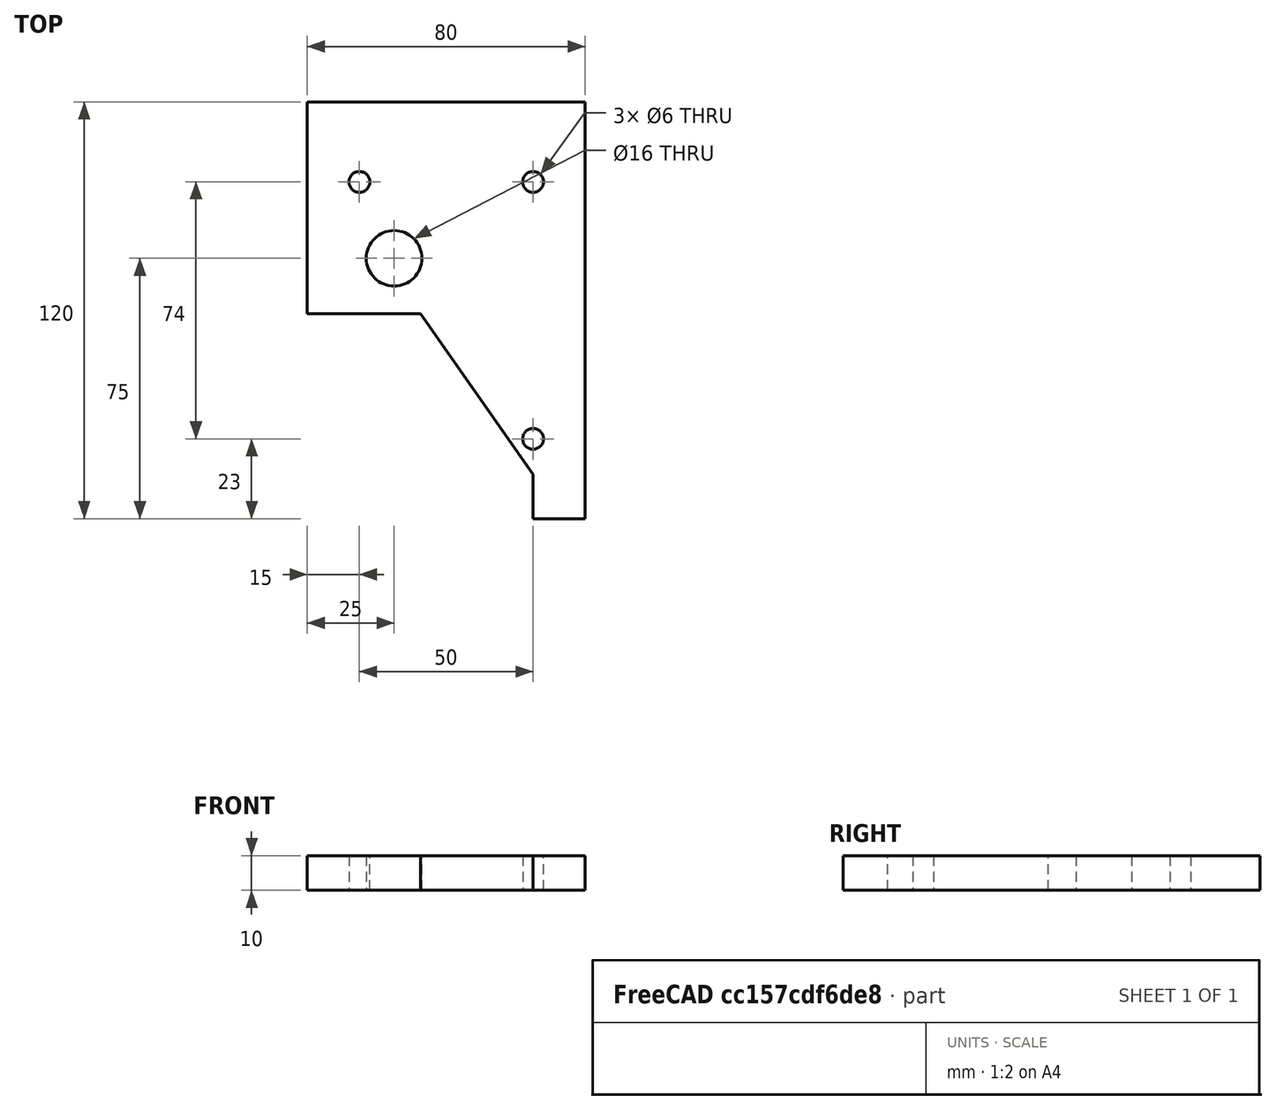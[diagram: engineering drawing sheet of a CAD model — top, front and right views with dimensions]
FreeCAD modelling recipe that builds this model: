
FCSTD DOCUMENT  (FreeCAD 0.19R24276 (Git))
Label: BLDC_holder_part4_up
License: All rights reserved
LicenseURL: http://en.wikipedia.org/wiki/All_rights_reserved
objects: Sketcher::SketchObject×1, PartDesign::Pad×1, PartDesign::Body×1
note: 4 computed .brp shape members not serialized (recipe doc carries the construction recipe); baked Part::Feature solids carry a one-line shape summary decoded from their .brp

FEATURE [Sketcher::SketchObject] Sketch  label="Sketch_L80x120"
  FullyConstrained = false
  MapMode = 5
  Support = -> [XY_Plane]
  sketch-geometry (36):
    g0: Circle CenterX=0 CenterY=0 CenterZ=0 NormalX=0 NormalY=0 NormalZ=1 AngleXU=0 Radius=8
    g1: Circle CenterX=0 CenterY=-30 CenterZ=0 NormalX=0 NormalY=0 NormalZ=1 AngleXU=0 Radius=11
    g2: LineSegment StartX=-25 StartY=45 StartZ=0 EndX=55 EndY=45 EndZ=0
    g3: LineSegment StartX=55 StartY=45 StartZ=0 EndX=55 EndY=-75 EndZ=0
    g4: LineSegment StartX=55 StartY=-75 StartZ=0 EndX=-25 EndY=-75 EndZ=0
    g5: LineSegment StartX=-25 StartY=-75 StartZ=0 EndX=-25 EndY=45 EndZ=0
    g6: Circle CenterX=-10 CenterY=-52 CenterZ=0 NormalX=0 NormalY=0 NormalZ=1 AngleXU=0 Radius=3
    g7: Circle CenterX=40 CenterY=-52 CenterZ=0 NormalX=0 NormalY=0 NormalZ=1 AngleXU=0 Radius=3
    g8: Circle CenterX=40 CenterY=22 CenterZ=0 NormalX=0 NormalY=0 NormalZ=1 AngleXU=0 Radius=3
    g9: Circle CenterX=-10 CenterY=22 CenterZ=0 NormalX=0 NormalY=0 NormalZ=1 AngleXU=0 Radius=3
    g10: Circle CenterX=0 CenterY=0 CenterZ=0 NormalX=0 NormalY=0 NormalZ=1 AngleXU=0 Radius=11
    g11: LineSegment StartX=14.5 StartY=-15.5 StartZ=0 EndX=-14.5 EndY=-15.5 EndZ=0
    g12: LineSegment StartX=-14.5 StartY=-15.5 StartZ=0 EndX=-14.5 EndY=-44.5 EndZ=0
    g13: LineSegment StartX=-14.5 StartY=-44.5 StartZ=0 EndX=14.5 EndY=-44.5 EndZ=0
    g14: LineSegment StartX=14.5 StartY=-44.5 StartZ=0 EndX=14.5 EndY=-15.5 EndZ=0
    g15: Circle CenterX=0 CenterY=-30 CenterZ=0 NormalX=0 NormalY=0 NormalZ=1 AngleXU=0 Radius=20.5061
    g16: LineSegment StartX=-44.3555 StartY=-59 StartZ=0 EndX=66.9363 EndY=-59 EndZ=0
    g17: LineSegment StartX=66.9363 StartY=-59 StartZ=0 EndX=66.9363 EndY=-67 EndZ=0
    g18: LineSegment StartX=66.9363 StartY=-67 StartZ=0 EndX=-44.3555 EndY=-67 EndZ=0
    g19: LineSegment StartX=-44.3555 StartY=-67 StartZ=0 EndX=-44.3555 EndY=-59 EndZ=0
    g20: LineSegment StartX=-44.3555 StartY=-63 StartZ=0 EndX=70.3737 EndY=-63 EndZ=0
    g21: LineSegment StartX=-44.3555 StartY=29 StartZ=0 EndX=66.9363 EndY=29 EndZ=0
    g22: LineSegment StartX=66.9363 StartY=29 StartZ=0 EndX=66.9363 EndY=37 EndZ=0
    g23: LineSegment StartX=66.9363 StartY=37 StartZ=0 EndX=-44.3555 EndY=37 EndZ=0
    g24: LineSegment StartX=-44.3555 StartY=37 StartZ=0 EndX=-44.3555 EndY=29 EndZ=0
    g25: LineSegment StartX=-44.3555 StartY=33 StartZ=0 EndX=70.3737 EndY=33 EndZ=0
    g26: LineSegment StartX=9.01067 StartY=-23.6907 StartZ=0 EndX=44.9379 EndY=-75 EndZ=0
    g27: LineSegment StartX=0 StartY=-30 StartZ=0 EndX=9.01067 EndY=-23.6907 EndZ=0
    g28: LineSegment StartX=0 StartY=-19 StartZ=0 EndX=-25 EndY=-19 EndZ=0
    g29: LineSegment StartX=0 StartY=-30 StartZ=0 EndX=0 EndY=-19 EndZ=0
    g30: LineSegment StartX=-25 StartY=45 StartZ=0 EndX=-25 EndY=-16 EndZ=0
    g31: LineSegment StartX=-25 StartY=-16 StartZ=0 EndX=7.62561 EndY=-16 EndZ=0
    g32: LineSegment StartX=7.62561 StartY=-16 StartZ=0 EndX=40 EndY=-62.2354 EndZ=0
    g33: LineSegment StartX=44.9379 StartY=-75 StartZ=0 EndX=55 EndY=-75 EndZ=0
    g34: LineSegment StartX=40 StartY=-75 StartZ=0 EndX=55 EndY=-75 EndZ=0
    g35: LineSegment StartX=40 StartY=-62.2354 StartZ=0 EndX=40 EndY=-75 EndZ=0
  constraints (90):
    c: Coincident(g0,g-1)
    c: Diameter(g0) = 16
    c: PointOnObject(g1,g-2)
    c: Diameter(g1) = 22
    c: DistanceY(g1,g0) = 30
    c: Coincident(g2,g3)
    c: Coincident(g3,g4)
    c: Coincident(g4,g5)
    c: Coincident(g5,g2)
    c: Horizontal(g2)
    c: Horizontal(g4)
    c: Vertical(g3)
    c: Vertical(g5)
    c: DistanceY(g4,g1) = 45
    c: DistanceY(g3,g2) = 120
    c: Horizontal(g9,g8)
    c: Horizontal(g6,g7)
    c: Vertical(g9,g6)
    c: Vertical(g8,g7)
    c: Diameter(g6) = 6
    c: Equal(g6,g8)
    c: Equal(g6,g9)
    c: Equal(g6,g7)
    c: DistanceY(g6,g1) = 22
    c: DistanceY(g0,g9) = 22
    c: Coincident(g10,g0)
    c: Diameter(g10) = 22
    c: DistanceX(g7,g3) = 15
    c: DistanceX(g4,g6) = 15
    c: DistanceX(g2,g2) = 80
    c: Coincident(g11,g12)
    c: Coincident(g12,g13)
    c: Coincident(g13,g14)
    c: Coincident(g14,g11)
    c: Equal(g11,g12)
    c: Equal(g11,g13)
    c: Equal(g11,g14)
    c: PointOnObject(g11,g15)
    c: PointOnObject(g12,g15)
    c: PointOnObject(g13,g15)
    c: PointOnObject(g14,g15)
    c: Coincident(g15,g1)
    c: DistanceY(g14,g14) = 29
    c: Vertical(g14)
    c: DistanceX(g2,g0) = 25
    c: Coincident(g16,g17)
    c: Coincident(g17,g18)
    c: Coincident(g18,g19)
    c: Coincident(g19,g16)
    c: Horizontal(g16)
    c: Horizontal(g18)
    c: Vertical(g17)
    c: Vertical(g19)
    c: Horizontal(g20)
    c: Symmetric(g16,g18,g20)
    c: DistanceY(g4,g20) = 12
    c: DistanceY(g19,g19) = 8
    c: Coincident(g21,g22)
    c: Coincident(g22,g23)
    c: Coincident(g23,g24)
    c: Coincident(g24,g21)
    c: Symmetric(g21,g23,g25)
    c: DistanceY(g25,g2) = 12
    c: Horizontal(g23)
    c: Horizontal(g21)
    c: Horizontal(g25)
    c: DistanceY(g24,g24) = 8
    c: PointOnObject(g26,g1)
    c: Tangent(g26,g1)
    c: Coincident(g27,g1)
    c: Coincident(g27,g26)
    c: Angle(g-1,g26) = 2.18166
    c: PointOnObject(g28,g1)
    c: Horizontal(g28)
    c: Coincident(g29,g1)
    c: Coincident(g29,g28)
    c: Vertical(g29)
    c: PointOnObject(g26,g4)
    c: PointOnObject(g28,g5)
    c: Coincident(g30,g2)
    c: Horizontal(g31)
    c: Coincident(g32,g31)
    c: Parallel(g26,g32)
    c: Coincident(g30,g31)
    c: Coincident(g33,g26)
    c: Coincident(g33,g3)
    c: PointOnObject(g35,g4)
    c: Coincident(g34,g35)
    c: Coincident(g34,g3)
    c: Coincident(g35,g32)
FEATURE [PartDesign::Pad] Pad
  Direction = (1,1,1)
  Length = 10
  Length2 = 100
  Profile = -> Sketch
  Type = 0
FEATURE [PartDesign::Body] Body
  Group = -> [Sketch,Pad]
  Origin = -> Origin
  Tip = -> Pad
